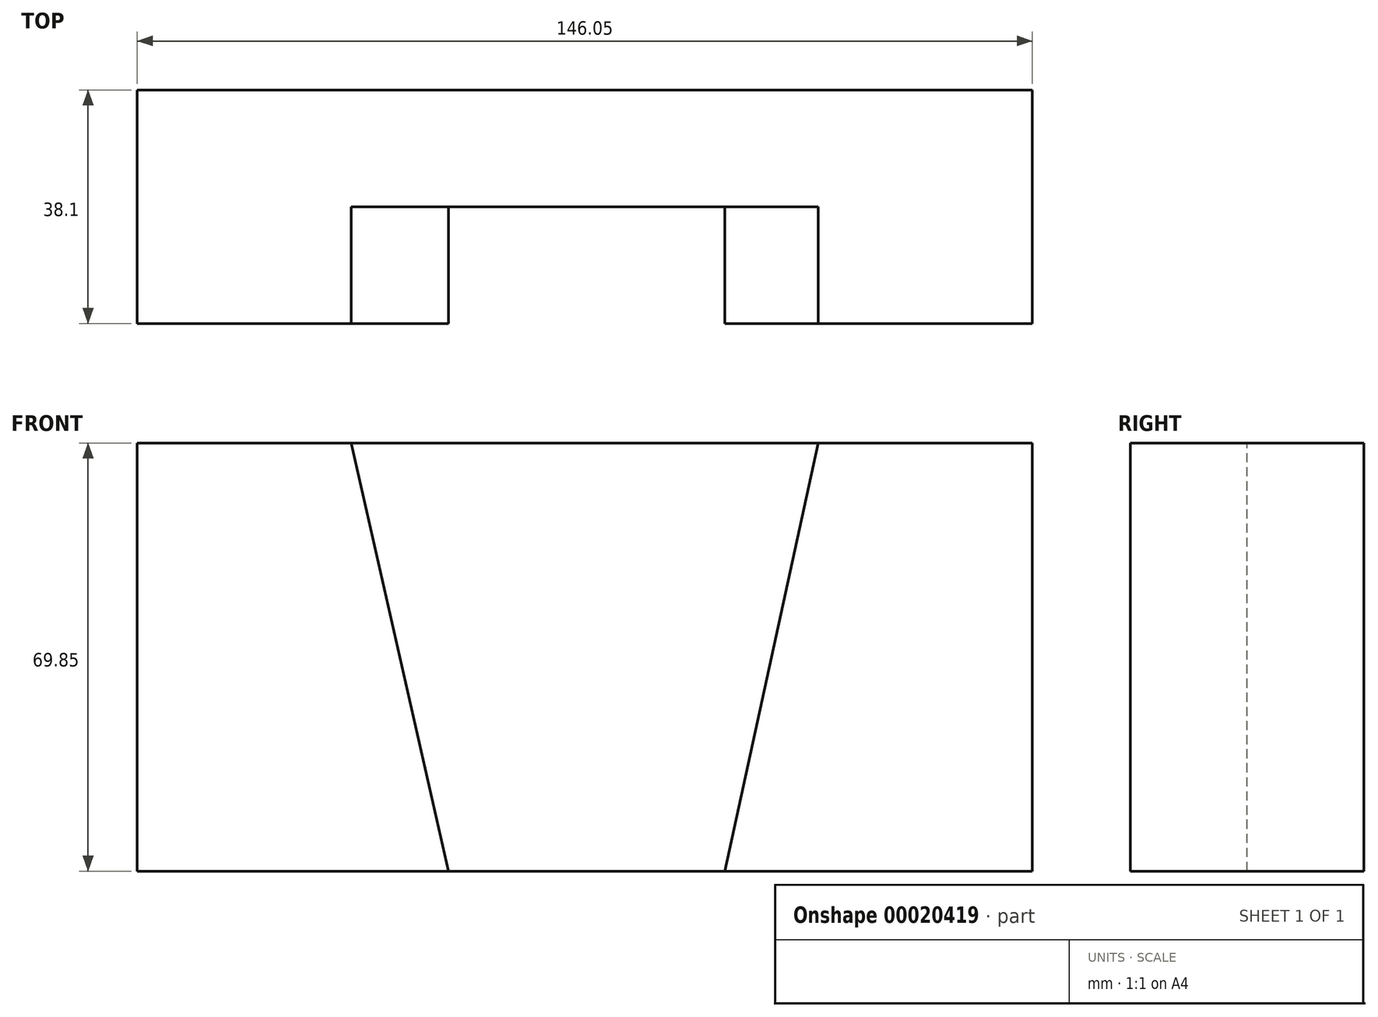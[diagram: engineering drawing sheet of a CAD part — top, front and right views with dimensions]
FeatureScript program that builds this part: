
annotation { "Feature Type Name" : "Feature", "Feature Type Description" : "" }
export const myFeature = defineFeature(function(context is Context, id is Id, definition is map)
    precondition{}
    {
        {
            var Q0;
            Q0=qCreatedBy(makeId("Front.planeOp"),FACE);
            var sketch = newSketch(context, id + "F0", { "sketchPlane" : qUnion([Q0])});
            skLineSegment(sketch, "E0.bottom", {"start": v(-73.65, 40.37) * mm, "end": v(72.4, 40.37) * mm});
            skLineSegment(sketch, "E0.top", {"start": v(-73.65, -29.48) * mm, "end": v(72.4, -29.48) * mm});
            skLineSegment(sketch, "E0.left", {"start": v(-73.65, 40.37) * mm, "end": v(-73.65, -29.48) * mm});
            skLineSegment(sketch, "E0.right", {"start": v(72.4, 40.37) * mm, "end": v(72.4, -29.48) * mm});
            skPoint(sketch, "E1", {"position": v(-22.85, -29.48) * mm});
            skPoint(sketch, "E2", {"position": v(21.6, -29.48) * mm});
            skPoint(sketch, "E3", {"position": v(-38.73, 40.37) * mm});
            skPoint(sketch, "E4", {"position": v(37.47, 40.37) * mm});
            skLineSegment(sketch, "E5", {"start": v(-38.73, 40.37) * mm, "end": v(-22.85, -29.48) * mm});
            skLineSegment(sketch, "E6", {"start": v(37.47, 40.37) * mm, "end": v(21.6, -32.35) * mm});
            skSolve(sketch);
        }
        {
            var Q0;
            {var subQ5=sQuery(id+"F0.wireOp",EDGE,"E0.right");Q0=makeQuery(id+"F0.imprint","IMPRINT",FACE,{"disambiguationData":[TD([[makeQuery(id+"F0.imprint","IMPRINT",EDGE,{"derivedFrom":subQ5}),-1.0]])]});}
            var Q1;
            {var subQ5=sQuery(id+"F0.wireOp",EDGE,"E5");Q1=makeQuery(id+"F0.imprint","IMPRINT",FACE,{"disambiguationData":[TD([[makeQuery(id+"F0.imprint","IMPRINT",EDGE,{"derivedFrom":subQ5}),1.0]])]});}
            var Q2;
            {var subQ1=sQuery(id+"F0.wireOp",EDGE,"E0.left");Q2=makeQuery(id+"F0.imprint","IMPRINT",FACE,{"disambiguationData":[TD([[makeQuery(id+"F0.imprint","IMPRINT",EDGE,{"derivedFrom":subQ1}),1.0]])]});}
            extrude(context, id + "F1", {"entities" : qUnion([Q0, Q1, Q2]), "depth" : 19.05 * mm});
        }
        {
            var Q0;
            {var subQ1=sQuery(id+"F0.wireOp",EDGE,"E0.left");Q0=makeQuery(id+"F0.imprint","IMPRINT",FACE,{"disambiguationData":[TD([[makeQuery(id+"F0.imprint","IMPRINT",EDGE,{"derivedFrom":subQ1}),1.0]])]});}
            extrude(context, id + "F2", {"entities" : qUnion([Q0]), "operationType" : NewBodyOperationType.ADD, "depth" : 38.1 * mm});
        }
        {
            var Q0;
            {var subQ5=sQuery(id+"F0.wireOp",EDGE,"E0.right");Q0=makeQuery(id+"F0.imprint","IMPRINT",FACE,{"disambiguationData":[TD([[makeQuery(id+"F0.imprint","IMPRINT",EDGE,{"derivedFrom":subQ5}),-1.0]])]});}
            extrude(context, id + "F3", {"entities" : qUnion([Q0]), "operationType" : NewBodyOperationType.ADD, "depth" : 38.1 * mm});
        }
    });
